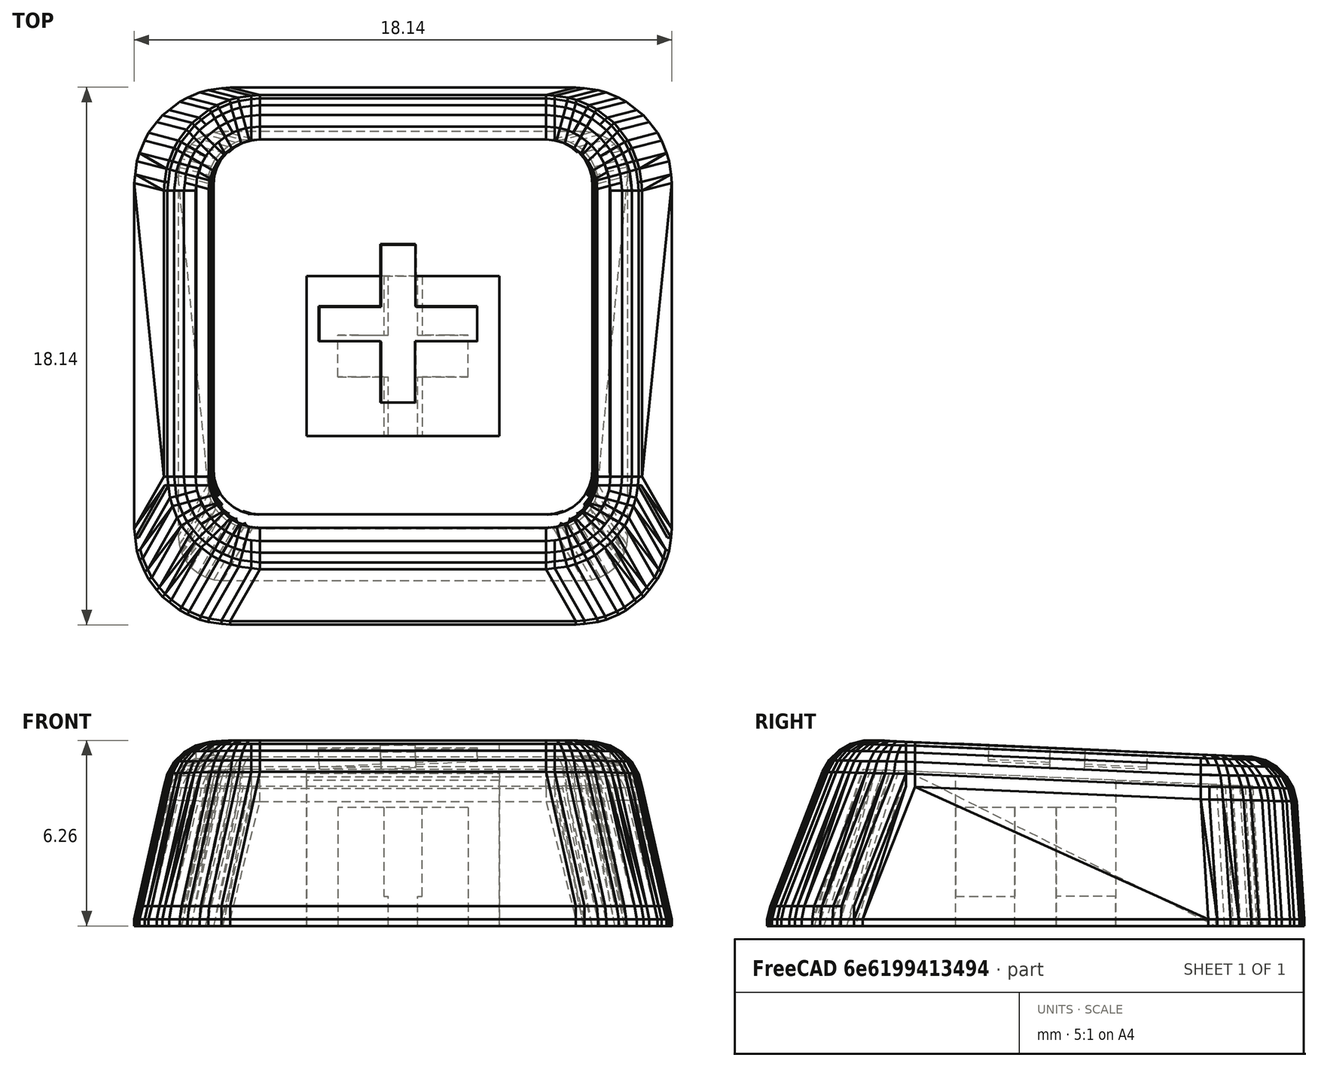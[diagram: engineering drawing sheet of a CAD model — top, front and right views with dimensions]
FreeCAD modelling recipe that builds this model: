
FCSTD DOCUMENT  (FreeCAD 0.18R16131 (Git))
Label: plus
License: All rights reserved
LicenseURL: http://en.wikipedia.org/wiki/All_rights_reserved
objects: Part::Box×4, Part::Feature×1, Part::MultiFuse×1, Part::Part2DObjectPython×1, Part::Extrusion×1, Part::Cut×1
note: 9 computed .brp shape members not serialized (recipe doc carries the construction recipe); baked Part::Feature solids carry a one-line shape summary decoded from their .brp

FEATURE [Part::Feature] Solid
  shape: bbox 18.13 x 18.13 x 6.262 mm, 1259 faces (baked)
FEATURE [Part::Box] Box  label="Cube"
  AttacherType = Attacher::AttachEngine3D
  Height = 1
  Length = 1
  Placement = pos=(0.5,-2.7,0) rot=(0,0,1;0rad)
  Width = 2
FEATURE [Part::Box] Box001  label="Cube001"
  AttacherType = Attacher::AttachEngine3D
  Height = 1
  Length = 1
  Placement = pos=(-1.5,0.7,0) rot=(0,0,1;0rad)
  Width = 2
FEATURE [Part::Box] Box002  label="Cube002"
  AttacherType = Attacher::AttachEngine3D
  Height = 1
  Length = 1
  Placement = pos=(-1.5,-2.7,0) rot=(0,0,1;0rad)
  Width = 2
FEATURE [Part::Box] Box003  label="Cube003"
  AttacherType = Attacher::AttachEngine3D
  Height = 1
  Length = 1
  Placement = pos=(0.5,0.7,0) rot=(0,0,1;0rad)
  Width = 2
FEATURE [Part::MultiFuse] Fusion
  Shapes = -> [Solid,Box002,Box001,Box,Box003]
FEATURE [Part::Part2DObjectPython] ShapeString  # Draft 2D object (typed FeaturePython)
  FontFile = <userpath>/A6E4-ED97/3dprinting/open-sans/OpenSans-Bold.ttf
  Placement = pos=(-3,-3,6) rot=(0,0,1;0rad)
  Size = 10
  String = +
  Tracking = 0
FEATURE [Part::Extrusion] Extrude001
  Base = -> ShapeString
  Dir = (0,0,1)
  DirMode = 2
  FaceMakerClass = Part::FaceMakerBullseye
  LengthFwd = 1
  LengthRev = 0
  Placement = pos=(0,0,-0.5) rot=(-0.707107,-0.707107,0;0.069813rad)
  Solid = false
  Symmetric = false
FEATURE [Part::Cut] Cut
  Base = -> Fusion
  Tool = -> Extrude001
